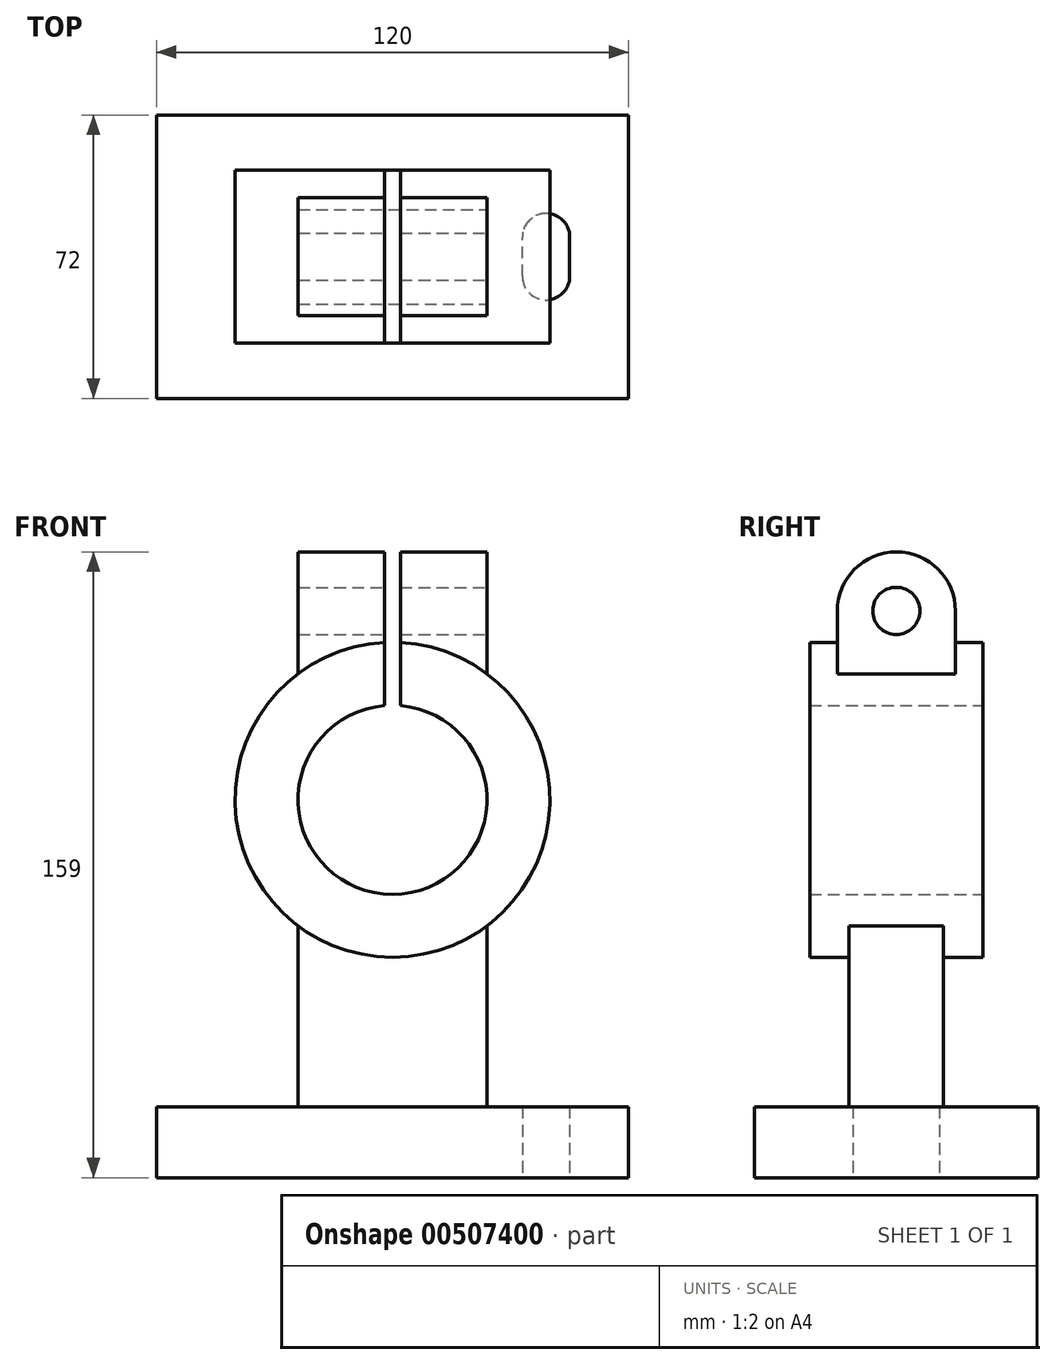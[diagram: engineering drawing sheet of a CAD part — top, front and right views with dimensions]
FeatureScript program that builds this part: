
annotation { "Feature Type Name" : "Feature", "Feature Type Description" : "" }
export const myFeature = defineFeature(function(context is Context, id is Id, definition is map)
    precondition{}
    {
        {
            var Q0;
            Q0=qCreatedBy(makeId("Front.planeOp"),FACE);
            var sketch = newSketch(context, id + "F0", { "sketchPlane" : qUnion([Q0])});
            skCircle(sketch, "E0", {"center": v(0, 0) * mm, "radius": 24 * mm});
            skCircle(sketch, "E1", {"center": v(0, 0) * mm, "radius": 40 * mm});
            skSolve(sketch);
        }
        {
            var Q0;
            Q0=makeQuery(id+"F0.imprint","IMPRINT",FACE,{"disambiguationData":[TD([[makeQuery(id+"F0.imprint","IMPRINT",EDGE,{"derivedFrom":sQuery(id+"F0.wireOp",EDGE,"E0")}),-1.0]])]});
            extrude(context, id + "F1", {"entities" : qUnion([Q0]), "endBound" : BoundingType.SYMMETRIC, "depth" : 44 * mm});
        }
        {
            var Q0;
            Q0=qCreatedBy(makeId("Front.planeOp"),FACE);
            var sketch = newSketch(context, id + "F2", { "sketchPlane" : qUnion([Q0])});
            skLineSegment(sketch, "E2.bottom", {"start": v(-24, -32) * mm, "end": v(24, -32) * mm});
            skLineSegment(sketch, "E2.top", {"start": v(-24, -96) * mm, "end": v(24, -96) * mm});
            skLineSegment(sketch, "E2.left", {"start": v(-24, -32) * mm, "end": v(-24, -96) * mm});
            skLineSegment(sketch, "E2.right", {"start": v(24, -32) * mm, "end": v(24, -96) * mm});
            skArc(sketch, "E3.0", {"start": v(-24, -32) * mm, "mid": v(0, -40) * mm, "end": v(24, -32) * mm, "construction": true});
            skSolve(sketch);
        }
        {
            var Q0;
            Q0 = qSketchRegion(id + "F2", true);
            extrude(context, id + "F3", {"entities" : qUnion([Q0]), "operationType" : NewBodyOperationType.ADD, "endBound" : BoundingType.SYMMETRIC, "depth" : 24 * mm});
        }
        {
            var Q0;
            Q0=makeQuery(id+"F3.opExtrude","SWEPT_FACE",FACE,{"disambiguationData":[OSD([sQuery(id+"F2.wireOp",EDGE,"E2.top")])]});
            var sketch = newSketch(context, id + "F4", { "sketchPlane" : qUnion([Q0])});
            skLineSegment(sketch, "E4.bottom", {"start": v(-60, 36) * mm, "end": v(60, 36) * mm});
            skLineSegment(sketch, "E4.top", {"start": v(-60, -36) * mm, "end": v(60, -36) * mm});
            skLineSegment(sketch, "E4.left", {"start": v(-60, 36) * mm, "end": v(-60, -36) * mm});
            skLineSegment(sketch, "E4.right", {"start": v(60, 36) * mm, "end": v(60, -36) * mm});
            skSolve(sketch);
        }
        {
            var Q0;
            Q0 = qSketchRegion(id + "F4", true);
            extrude(context, id + "F5", {"entities" : qUnion([Q0]), "operationType" : NewBodyOperationType.ADD, "oppositeDirection" : true, "depth" : 18 * mm});
        }
        {
            var Q0;
            Q0=qCreatedBy(makeId("Right.planeOp"),FACE);
            var sketch = newSketch(context, id + "F6", { "sketchPlane" : qUnion([Q0])});
            skLineSegment(sketch, "E5.top", {"start": v(15, 25) * mm, "end": v(-15, 25) * mm});
            skLineSegment(sketch, "E5.left", {"start": v(15, 48) * mm, "end": v(15, 25) * mm});
            skLineSegment(sketch, "E5.right", {"start": v(-15, 48) * mm, "end": v(-15, 25) * mm});
            skArc(sketch, "E6", {"start": v(15, 48) * mm, "mid": v(0, 63) * mm, "end": v(-15, 48) * mm});
            skSolve(sketch);
        }
        {
            var Q0;
            Q0 = qSketchRegion(id + "F6", true);
            extrude(context, id + "F7", {"entities" : qUnion([Q0]), "operationType" : NewBodyOperationType.ADD, "endBound" : BoundingType.SYMMETRIC, "depth" : 48 * mm});
        }
        {
            var Q0;
            Q0=makeQuery(id+"F7.opExtrude","CAP_FACE",FACE,{"disambiguationData":[OSD([sQuery(id+"F6.wireOp",EDGE,"E5.top"),sQuery(id+"F6.wireOp",EDGE,"E5.left"),sQuery(id+"F6.wireOp",EDGE,"E5.right"),sQuery(id+"F6.wireOp",EDGE,"E6")])],"isStart":false});
            var sketch = newSketch(context, id + "F8", { "sketchPlane" : qUnion([Q0])});
            skCircle(sketch, "E7", {"center": v(0, 48) * mm, "radius": 6 * mm});
            skSolve(sketch);
        }
        {
            var Q0;
            Q0 = qSketchRegion(id + "F8", true);
            extrude(context, id + "F9", {"entities" : qUnion([Q0]), "operationType" : NewBodyOperationType.REMOVE, "endBound" : BoundingType.THROUGH_ALL, "oppositeDirection" : true, "depth" : 27 * mm});
        }
        {
            var Q0;
            Q0=makeQuery(id+"F5.boolean.opBoolean","MERGE",FACE,{"derivedFrom":[makeQuery(id+"F3.opExtrude","SWEPT_FACE",FACE,{"disambiguationData":[OSD([sQuery(id+"F2.wireOp",EDGE,"E2.top")])]}),makeQuery(id+"F5.opExtrude","CAP_FACE",FACE,{"disambiguationData":[OSD([sQuery(id+"F4.wireOp",EDGE,"E4.bottom"),sQuery(id+"F4.wireOp",EDGE,"E4.top"),sQuery(id+"F4.wireOp",EDGE,"E4.left"),sQuery(id+"F4.wireOp",EDGE,"E4.right")])],"isStart":true})]});
            var sketch = newSketch(context, id + "F10", { "sketchPlane" : qUnion([Q0])});
            skLineSegment(sketch, "E8.bottom", {"start": v(45, 5) * mm, "end": v(33, 5) * mm, "construction": true});
            skLineSegment(sketch, "E8.top", {"start": v(45, -5) * mm, "end": v(33, -5) * mm, "construction": true});
            skLineSegment(sketch, "E8.left", {"start": v(45, 5) * mm, "end": v(45, -5) * mm});
            skLineSegment(sketch, "E8.right", {"start": v(33, 5) * mm, "end": v(33, -5) * mm});
            skArc(sketch, "E9", {"start": v(45, 5) * mm, "mid": v(39, 11) * mm, "end": v(33, 5) * mm});
            skArc(sketch, "E10", {"start": v(45, -5) * mm, "mid": v(39, -11) * mm, "end": v(33, -5) * mm});
            skSolve(sketch);
        }
        {
            var Q0;
            Q0 = qSketchRegion(id + "F10", true);
            extrude(context, id + "F11", {"entities" : qUnion([Q0]), "operationType" : NewBodyOperationType.REMOVE, "oppositeDirection" : true, "depth" : 25 * mm});
        }
        {
            var Q0;
            Q0=qCreatedBy(makeId("Front.planeOp"),FACE);
            var sketch = newSketch(context, id + "F12", { "sketchPlane" : qUnion([Q0])});
            skLineSegment(sketch, "E11.bottom", {"start": v(2, 20) * mm, "end": v(-2, 20) * mm});
            skLineSegment(sketch, "E11.top", {"start": v(2, 70) * mm, "end": v(-2, 70) * mm});
            skLineSegment(sketch, "E11.left", {"start": v(2, 20) * mm, "end": v(2, 70) * mm});
            skLineSegment(sketch, "E11.right", {"start": v(-2, 20) * mm, "end": v(-2, 70) * mm});
            skPoint(sketch, "E11.middle", {"position": v(0, 45) * mm});
            skSolve(sketch);
        }
        {
            var Q0;
            Q0 = qSketchRegion(id + "F12", true);
            extrude(context, id + "F13", {"entities" : qUnion([Q0]), "operationType" : NewBodyOperationType.REMOVE, "endBound" : BoundingType.SYMMETRIC, "oppositeDirection" : true, "depth" : 50 * mm});
        }
    });
